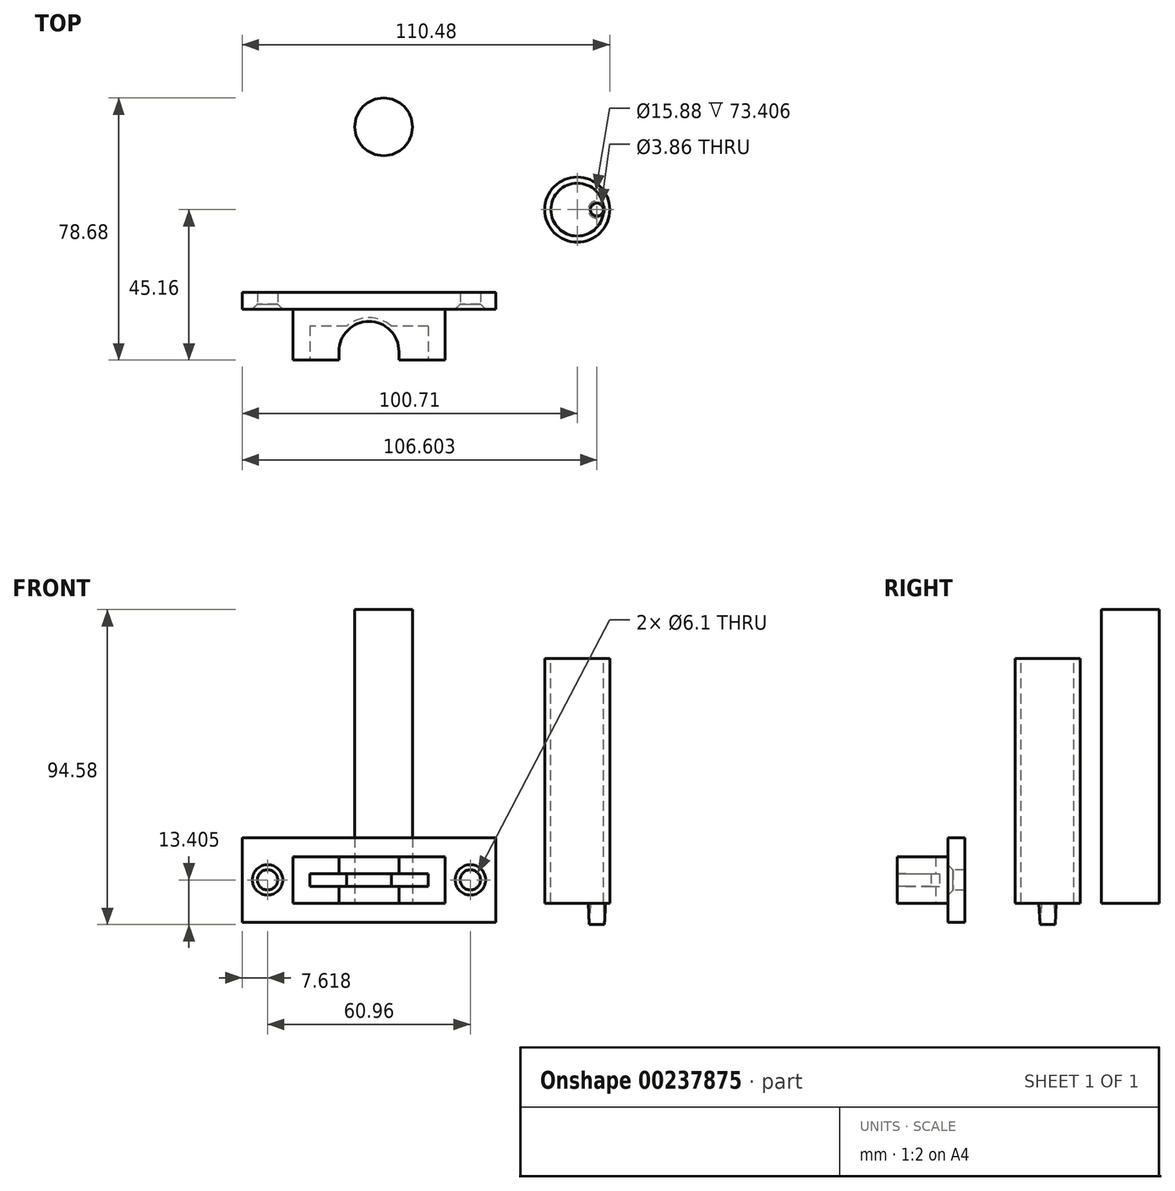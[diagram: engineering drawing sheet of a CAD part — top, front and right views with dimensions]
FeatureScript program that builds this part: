
annotation { "Feature Type Name" : "Feature", "Feature Type Description" : "" }
export const myFeature = defineFeature(function(context is Context, id is Id, definition is map)
    precondition{}
    {
        {
            var Q0;
            Q0=qCreatedBy(makeId("Top.planeOp"),FACE);
            var sketch = newSketch(context, id + "F0", { "sketchPlane" : qUnion([Q0])});
            skCircle(sketch, "E0", {"center": v(0, 0) * mm, "radius": 9.77 * mm});
            skCircle(sketch, "E1", {"center": v(5.9, 0) * mm, "radius": 2.6 * mm});
            skCircle(sketch, "E2", {"center": v(5.9, 0) * mm, "radius": 1.93 * mm});
            skSolve(sketch);
        }
        {
            var Q0;
            Q0=makeQuery(id+"F0.imprint","IMPRINT",FACE,{"disambiguationData":[TD([[makeQuery(id+"F0.imprint","IMPRINT",EDGE,{"derivedFrom":sQuery(id+"F0.wireOp",EDGE,"E0")}),1.0]])]});
            var Q1;
            Q1=makeQuery(id+"F0.imprint","IMPRINT",FACE,{"disambiguationData":[TD([[makeQuery(id+"F0.imprint","IMPRINT",EDGE,{"derivedFrom":sQuery(id+"F0.wireOp",EDGE,"E2")}),1.0]])]});
            var Q2;
            Q2=makeQuery(id+"F0.imprint","IMPRINT",FACE,{"disambiguationData":[TD([[makeQuery(id+"F0.imprint","IMPRINT",EDGE,{"derivedFrom":sQuery(id+"F0.wireOp",EDGE,"E1")}),1.0]])]});
            extrude(context, id + "F1", {"entities" : qUnion([Q0, Q1, Q2]), "depth" : 73.53 * mm});
        }
        {
            var Q0;
            Q0=makeQuery(id+"F1.opExtrude","CAP_FACE",FACE,{"disambiguationData":[OSD([sQuery(id+"F0.wireOp",EDGE,"E0")])],"isStart":false});
            var sketch = newSketch(context, id + "F2", { "sketchPlane" : qUnion([Q0])});
            skCircle(sketch, "E3", {"center": v(0, 0) * mm, "radius": 7.94 * mm});
            skSolve(sketch);
        }
        {
            var Q0;
            Q0=makeQuery(id+"F2.imprint","IMPRINT",FACE,{"disambiguationData":[TD([[makeQuery(id+"F2.imprint","IMPRINT",EDGE,{"derivedFrom":sQuery(id+"F2.wireOp",EDGE,"E3")}),1.0]])]});
            extrude(context, id + "F3", {"entities" : qUnion([Q0]), "operationType" : NewBodyOperationType.REMOVE, "oppositeDirection" : true, "depth" : 73.4 * mm});
        }
        {
            var Q0;
            Q0=makeQuery(id+"F0.imprint","IMPRINT",FACE,{"disambiguationData":[TD([[makeQuery(id+"F0.imprint","IMPRINT",EDGE,{"derivedFrom":sQuery(id+"F0.wireOp",EDGE,"E1")}),1.0]])]});
            extrude(context, id + "F4", {"entities" : qUnion([Q0]), "operationType" : NewBodyOperationType.ADD, "oppositeDirection" : true, "depth" : 12.7 * mm, "hasDraft" : true, "draftAngle" : 3 * degree, "draftPullDirection" : true});
        }
        {
            var Q0;
            Q0=makeQuery(id+"F0.imprint","IMPRINT",FACE,{"disambiguationData":[TD([[makeQuery(id+"F0.imprint","IMPRINT",EDGE,{"derivedFrom":sQuery(id+"F0.wireOp",EDGE,"E2")}),1.0]])]});
            extrude(context, id + "F5", {"entities" : qUnion([Q0]), "operationType" : NewBodyOperationType.REMOVE, "depth" : 25.4 * mm});
        }
        {
            var Q0;
            Q0=qCreatedBy(makeId("Top.planeOp"),FACE);
            var sketch = newSketch(context, id + "F6", { "sketchPlane" : qUnion([Q0])});
            skCircle(sketch, "E4", {"center": v(-58.19, 24.86) * mm, "radius": 8.66 * mm});
            skSolve(sketch);
        }
        {
            var Q0;
            Q0 = qSketchRegion(id + "F6", true);
            extrude(context, id + "F7", {"entities" : qUnion([Q0]), "depth" : 88.16 * mm});
        }
        {
            var Q0;
            Q0=qCreatedBy(makeId("Top.planeOp"),FACE);
            var sketch = newSketch(context, id + "F8", { "sketchPlane" : qUnion([Q0])});
            skCircle(sketch, "E5", {"center": v(-62.61, -42.62) * mm, "radius": 9.02 * mm});
            skCircle(sketch, "E6", {"center": v(-62.61, -42.62) * mm, "radius": 10.16 * mm});
            skLineSegment(sketch, "E7.top", {"start": v(-39.75, -29.92) * mm, "end": v(-85.47, -29.92) * mm});
            skLineSegment(sketch, "E7.left", {"start": v(-39.75, -45.16) * mm, "end": v(-39.75, -29.92) * mm});
            skLineSegment(sketch, "E7.right", {"start": v(-85.47, -45.16) * mm, "end": v(-85.47, -29.92) * mm});
            skPoint(sketch, "E8", {"position": v(-62.61, -45.16) * mm});
            skLineSegment(sketch, "E9", {"start": v(-85.47, -45.16) * mm, "end": v(-39.75, -45.16) * mm});
            skLineSegment(sketch, "E10", {"start": v(-72.77, -42.62) * mm, "end": v(-72.77, -45.16) * mm});
            skLineSegment(sketch, "E11", {"start": v(-52.45, -42.62) * mm, "end": v(-52.45, -45.16) * mm});
            skLineSegment(sketch, "E12.bottom", {"start": v(-80.4, -45.16) * mm, "end": v(-44.83, -45.16) * mm});
            skLineSegment(sketch, "E12.top", {"start": v(-80.4, -35) * mm, "end": v(-44.83, -35) * mm});
            skLineSegment(sketch, "E12.left", {"start": v(-80.4, -45.16) * mm, "end": v(-80.4, -35) * mm});
            skLineSegment(sketch, "E12.right", {"start": v(-44.83, -45.16) * mm, "end": v(-44.83, -35) * mm});
            skLineSegment(sketch, "E13", {"start": v(-71.63, -42.62) * mm, "end": v(-71.63, -45.16) * mm, "construction": true});
            skLineSegment(sketch, "E14", {"start": v(-53.6, -42.62) * mm, "end": v(-53.6, -45.16) * mm, "construction": true});
            skLineSegment(sketch, "E15.bottom", {"start": v(-71.63, -42.62) * mm, "end": v(-53.6, -42.62) * mm});
            skLineSegment(sketch, "E15.top", {"start": v(-71.63, -45.16) * mm, "end": v(-53.6, -45.16) * mm});
            skLineSegment(sketch, "E15.left", {"start": v(-71.63, -42.62) * mm, "end": v(-71.63, -45.16) * mm});
            skLineSegment(sketch, "E15.right", {"start": v(-53.6, -42.62) * mm, "end": v(-53.6, -45.16) * mm});
            skSolve(sketch);
        }
        {
            var Q0;
            {var subQ1=sQuery(id+"F8.wireOp",EDGE,"E7.right");Q0=makeQuery(id+"F8.imprint","IMPRINT",FACE,{"disambiguationData":[TD([[makeQuery(id+"F8.imprint","IMPRINT",EDGE,{"derivedFrom":subQ1}),-1.0]])]});}
            var Q1;
            {var subQ1=sQuery(id+"F8.wireOp",EDGE,"E7.left");Q1=makeQuery(id+"F8.imprint","IMPRINT",FACE,{"disambiguationData":[TD([[makeQuery(id+"F8.imprint","IMPRINT",EDGE,{"derivedFrom":subQ1}),1.0]])]});}
            var Q2;
            {var subQ0=sQuery(id+"F8.wireOp",EDGE,"E10");Q2=makeQuery(id+"F8.imprint","IMPRINT",FACE,{"disambiguationData":[TD([[makeQuery(id+"F8.imprint","IMPRINT",EDGE,{"derivedFrom":subQ0}),1.0]])]});}
            var Q3;
            {var subQ0=sQuery(id+"F8.wireOp",EDGE,"E11");Q3=makeQuery(id+"F8.imprint","IMPRINT",FACE,{"disambiguationData":[TD([[makeQuery(id+"F8.imprint","IMPRINT",EDGE,{"derivedFrom":subQ0}),-1.0]])]});}
            var Q4;
            {var subQ8=sQuery(id+"F8.wireOp",EDGE,"b746b15b-b173-4421-9281-08ae0f6e52980.MirrorCS");Q4=makeQuery(id+"F8.imprint","IMPRINT",FACE,{"disambiguationData":[TD([[makeQuery(id+"F8.imprint","IMPRINT",EDGE,{"derivedFrom":subQ8}),1.0]])]});}
            var Q5;
            {var subQ1=sQuery(id+"F8.wireOp",EDGE,"E10");Q5=makeQuery(id+"F8.imprint","IMPRINT",FACE,{"disambiguationData":[TD([[makeQuery(id+"F8.imprint","IMPRINT",EDGE,{"derivedFrom":subQ1}),-1.0]])]});}
            var Q6;
            {var subQ1=sQuery(id+"F8.wireOp",EDGE,"E11");Q6=makeQuery(id+"F8.imprint","IMPRINT",FACE,{"disambiguationData":[TD([[makeQuery(id+"F8.imprint","IMPRINT",EDGE,{"derivedFrom":subQ1}),1.0]])]});}
            var Q7;
            {var subQ0=sQuery(id+"F8.wireOp",EDGE,"E12.top");var subQ1=sQuery(id+"F8.wireOp",EDGE,"E5");var subQ2=makeQuery(id+"F8.imprint","INTERSECT",VERTEX,{"disambiguationData":[OD(0.0)],"derivedFrom":[subQ1,subQ0]});Q7=makeQuery(id+"F8.imprint","IMPRINT",FACE,{"disambiguationData":[TD([[makeQuery(id+"F8.imprint","IMPRINT",EDGE,{"disambiguationData":[TD([[subQ2,-1.0]])],"derivedFrom":subQ1}),-1.0]])]});}
            var Q8;
            {var subQ4=sQuery(id+"F8.wireOp",EDGE,"E12.top");var subQ6=sQuery(id+"F8.wireOp",EDGE,"E5");var subQ7=makeQuery(id+"F8.imprint","INTERSECT",VERTEX,{"disambiguationData":[OD(1.0)],"derivedFrom":[subQ6,subQ4]});Q8=makeQuery(id+"F8.imprint","IMPRINT",FACE,{"disambiguationData":[TD([[makeQuery(id+"F8.imprint","IMPRINT",EDGE,{"disambiguationData":[TD([[subQ7,-1.0]])],"derivedFrom":subQ6}),-1.0]])]});}
            var Q9;
            {var subQ0=sQuery(id+"F8.wireOp",EDGE,"E15.right");Q9=makeQuery(id+"F8.imprint","IMPRINT",FACE,{"disambiguationData":[TD([[makeQuery(id+"F8.imprint","IMPRINT",EDGE,{"derivedFrom":subQ0}),1.0]])]});}
            extrude(context, id + "F9", {"entities" : qUnion([Q0, Q1, Q2, Q3, Q4, Q5, Q6, Q7, Q8, Q9]), "depth" : 5.08 * mm});
        }
        {
            var Q0;
            {var subQ0=sQuery(id+"F8.wireOp",EDGE,"E7.right");Q0=makeQuery(id+"F8.imprint","IMPRINT",FACE,{"disambiguationData":[TD([[makeQuery(id+"F8.imprint","IMPRINT",EDGE,{"derivedFrom":subQ0}),-1.0]])]});}
            var Q1;
            {var subQ3=sQuery(id+"F8.wireOp",EDGE,"E7.left");Q1=makeQuery(id+"F8.imprint","IMPRINT",FACE,{"disambiguationData":[TD([[makeQuery(id+"F8.imprint","IMPRINT",EDGE,{"derivedFrom":subQ3}),1.0]])]});}
            extrude(context, id + "F10", {"entities" : qUnion([Q0, Q1]), "operationType" : NewBodyOperationType.ADD, "depth" : 8.9 * mm});
        }
        {
            var Q0;
            {var subQ3=sQuery(id+"F8.wireOp",EDGE,"E7.right");Q0=makeQuery(id+"F8.imprint","IMPRINT",FACE,{"disambiguationData":[TD([[makeQuery(id+"F8.imprint","IMPRINT",EDGE,{"derivedFrom":subQ3}),-1.0]])]});}
            var Q1;
            {var subQ3=sQuery(id+"F8.wireOp",EDGE,"E7.left");Q1=makeQuery(id+"F8.imprint","IMPRINT",FACE,{"disambiguationData":[TD([[makeQuery(id+"F8.imprint","IMPRINT",EDGE,{"derivedFrom":subQ3}),1.0]])]});}
            var Q2;
            {var subQ1=sQuery(id+"F8.wireOp",EDGE,"E11");Q2=makeQuery(id+"F8.imprint","IMPRINT",FACE,{"disambiguationData":[TD([[makeQuery(id+"F8.imprint","IMPRINT",EDGE,{"derivedFrom":subQ1}),1.0]])]});}
            var Q3;
            {var subQ4=sQuery(id+"F8.wireOp",EDGE,"b746b15b-b173-4421-9281-08ae0f6e52980.MirrorCS");Q3=makeQuery(id+"F8.imprint","IMPRINT",FACE,{"disambiguationData":[TD([[makeQuery(id+"F8.imprint","IMPRINT",EDGE,{"derivedFrom":subQ4}),1.0]])]});}
            var Q4;
            {var subQ0=sQuery(id+"F8.wireOp",EDGE,"E12.top");var subQ1=sQuery(id+"F8.wireOp",EDGE,"E5");var subQ2=makeQuery(id+"F8.imprint","INTERSECT",VERTEX,{"disambiguationData":[OD(0.0)],"derivedFrom":[subQ1,subQ0]});Q4=makeQuery(id+"F8.imprint","IMPRINT",FACE,{"disambiguationData":[TD([[makeQuery(id+"F8.imprint","IMPRINT",EDGE,{"disambiguationData":[TD([[subQ2,-1.0]])],"derivedFrom":subQ1}),-1.0]])]});}
            var Q5;
            {var subQ4=sQuery(id+"F8.wireOp",EDGE,"oYCFffuB-2gqM-RgqH-B8UD-AKh6t3XLDEdo");Q5=makeQuery(id+"F8.imprint","IMPRINT",FACE,{"disambiguationData":[TD([[makeQuery(id+"F8.imprint","IMPRINT",EDGE,{"derivedFrom":subQ4}),-1.0]])]});}
            var Q6;
            {var subQ1=sQuery(id+"F8.wireOp",EDGE,"E10");Q6=makeQuery(id+"F8.imprint","IMPRINT",FACE,{"disambiguationData":[TD([[makeQuery(id+"F8.imprint","IMPRINT",EDGE,{"derivedFrom":subQ1}),-1.0]])]});}
            var Q7;
            {var subQ0=sQuery(id+"F8.wireOp",EDGE,"E10");Q7=makeQuery(id+"F8.imprint","IMPRINT",FACE,{"disambiguationData":[TD([[makeQuery(id+"F8.imprint","IMPRINT",EDGE,{"derivedFrom":subQ0}),1.0]])]});}
            var Q8;
            {var subQ0=sQuery(id+"F8.wireOp",EDGE,"E11");Q8=makeQuery(id+"F8.imprint","IMPRINT",FACE,{"disambiguationData":[TD([[makeQuery(id+"F8.imprint","IMPRINT",EDGE,{"derivedFrom":subQ0}),-1.0]])]});}
            var Q9;
            {var subQ6=sQuery(id+"F8.wireOp",EDGE,"E15.left");Q9=makeQuery(id+"F8.imprint","IMPRINT",FACE,{"disambiguationData":[TD([[makeQuery(id+"F8.imprint","IMPRINT",EDGE,{"derivedFrom":subQ6}),-1.0]])]});}
            var Q10;
            {var subQ0=sQuery(id+"F8.wireOp",EDGE,"E15.right");Q10=makeQuery(id+"F8.imprint","IMPRINT",FACE,{"disambiguationData":[TD([[makeQuery(id+"F8.imprint","IMPRINT",EDGE,{"derivedFrom":subQ0}),1.0]])]});}
            extrude(context, id + "F11", {"entities" : qUnion([Q0, Q1, Q2, Q3, Q4, Q5, Q6, Q7, Q8, Q9, Q10]), "operationType" : NewBodyOperationType.ADD, "depth" : 13.97 * mm, "hasSecondDirection" : true, "secondDirectionOppositeDirection" : false, "secondDirectionDepth" : 8.9 * mm});
        }
        {
            var Q0;
            {var subQ0=sQuery(id+"F8.wireOp",EDGE,"E7.top");Q0=makeQuery(id+"F11.boolean.opBoolean","MERGE",FACE,{"derivedFrom":[makeQuery(id+"F10.boolean.opBoolean","MERGE",FACE,{"derivedFrom":[makeQuery(id+"F9.opExtrude","SWEPT_FACE",FACE,{"disambiguationData":[OSD([subQ0])]}),makeQuery(id+"F10.opExtrude","SWEPT_FACE",FACE,{"disambiguationData":[OSD([subQ0])]})]}),makeQuery(id+"F11.opExtrude","SWEPT_FACE",FACE,{"disambiguationData":[OSD([subQ0])]})]});}
            var sketch = newSketch(context, id + "F12", { "sketchPlane" : qUnion([Q0])});
            skLineSegment(sketch, "E16.bottom", {"start": v(100.71, -5.71) * mm, "end": v(24.51, -5.71) * mm});
            skLineSegment(sketch, "E16.top", {"start": v(100.71, 19.69) * mm, "end": v(24.51, 19.69) * mm});
            skLineSegment(sketch, "E16.left", {"start": v(100.71, -5.72) * mm, "end": v(100.71, 19.69) * mm});
            skLineSegment(sketch, "E16.right", {"start": v(24.51, -5.72) * mm, "end": v(24.51, 19.69) * mm});
            skPoint(sketch, "E16.middle", {"position": v(62.61, 6.99) * mm});
            skPoint(sketch, "E16.middle.positionSnap0", {"position": v(85.47, 6.99) * mm});
            skPoint(sketch, "E16.middle.positionSnap1", {"position": v(62.61, 0) * mm});
            skPoint(sketch, "E16.centerSnap0", {"position": v(85.47, 6.99) * mm});
            skPoint(sketch, "E16.centerSnap1", {"position": v(62.61, 0) * mm});
            skLineSegment(sketch, "E17", {"start": v(85.47, 6.99) * mm, "end": v(100.71, 6.99) * mm, "construction": true});
            skCircle(sketch, "E18", {"center": v(93.1, 6.99) * mm, "radius": 3.05 * mm});
            skLineSegment(sketch, "E19", {"start": v(62.61, 0) * mm, "end": v(62.61, 6.99) * mm, "construction": true});
            skCircle(sketch, "E20.MirrorC", {"center": v(32.13, 6.98) * mm, "radius": 3.05 * mm});
            skSolve(sketch);
        }
        {
            var Q0;
            Q0=makeQuery(id+"F12.imprint","IMPRINT",FACE,{"disambiguationData":[TD([[makeQuery(id+"F12.imprint","IMPRINT",EDGE,{"derivedFrom":sQuery(id+"F12.wireOp",EDGE,"E16.bottom")}),-1.0]])]});
            var Q1;
            {var subQ0=sQuery(id+"F8.wireOp",EDGE,"E7.top");Q1=makeQuery(id+"F12.imprint","IMPRINT",FACE,{"disambiguationData":[TD([[makeQuery(id+"F12.imprint","IMPRINT",EDGE,{"derivedFrom":makeQuery(id+"F9.opExtrude","CAP_EDGE",EDGE,{"disambiguationData":[OSD([subQ0])],"isStart":true})}),1.0]])]});}
            extrude(context, id + "F13", {"entities" : qUnion([Q0, Q1]), "operationType" : NewBodyOperationType.ADD, "depth" : 5.08 * mm});
        }
        {
            var Q0;
            Q0=makeQuery(id+"F13.opExtrude","CAP_EDGE",EDGE,{"disambiguationData":[OSD([sQuery(id+"F12.wireOp",EDGE,"E18")])],"isStart":true});
            var Q1;
            Q1=makeQuery(id+"F13.opExtrude","CAP_EDGE",EDGE,{"disambiguationData":[OSD([sQuery(id+"F12.wireOp",EDGE,"E20.MirrorC")])],"isStart":true});
            chamfer(context, id + "F14", {"entities" : qUnion([Q0, Q1]), "width" : 1.52 * mm, "tangentPropagation" : true});
        }
    });
